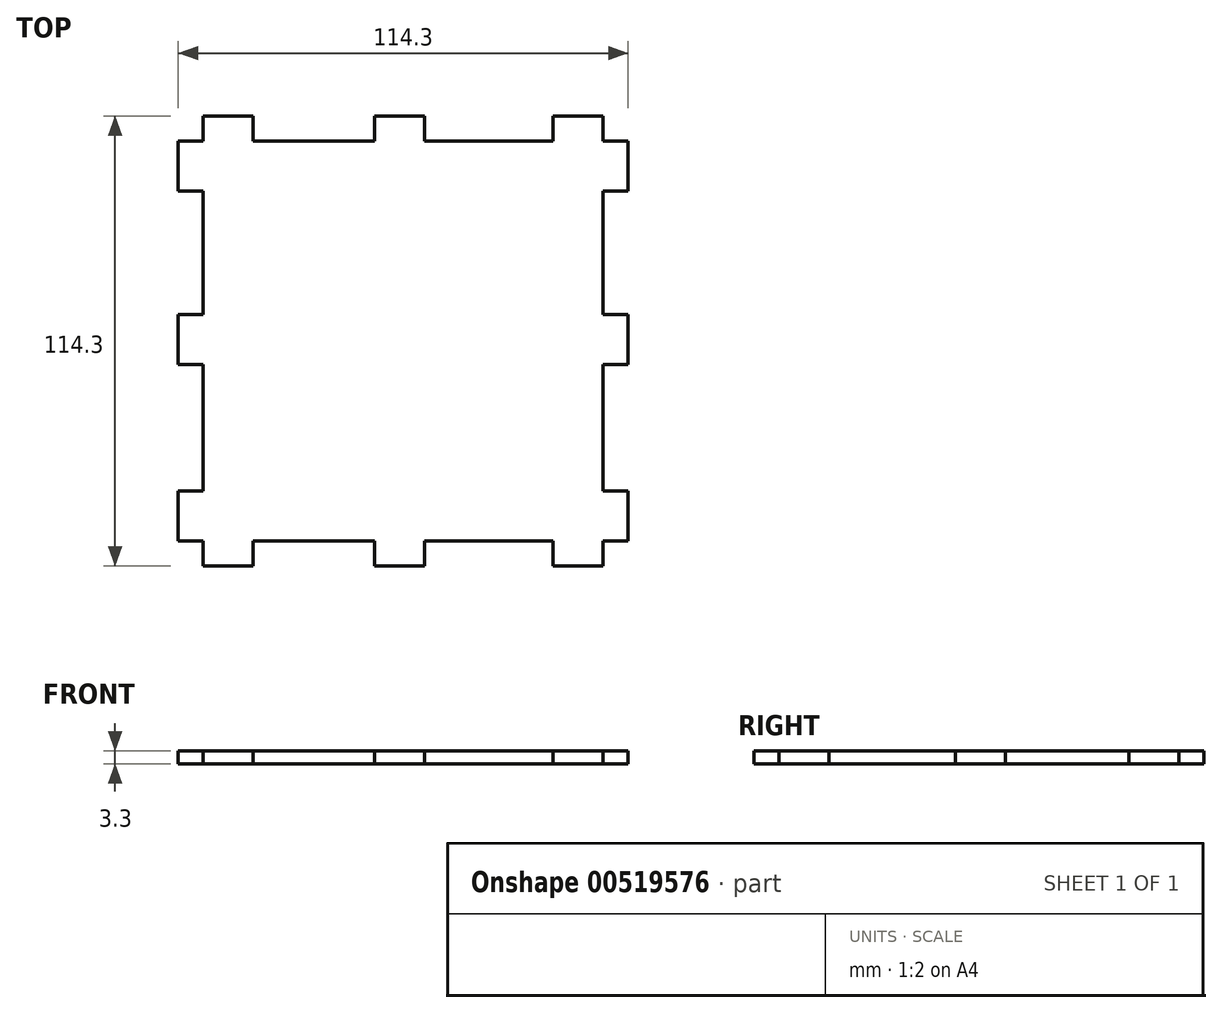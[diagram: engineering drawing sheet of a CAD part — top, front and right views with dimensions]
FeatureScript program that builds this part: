
annotation { "Feature Type Name" : "Feature", "Feature Type Description" : "" }
export const myFeature = defineFeature(function(context is Context, id is Id, definition is map)
    precondition{}
    {
        {
            var Q0;
            Q0=qCreatedBy(makeId("Top.planeOp"),FACE);
            var sketch = newSketch(context, id + "F0", { "sketchPlane" : qUnion([Q0])});
            skPoint(sketch, "E0.middle", {"position": v(0, 0) * mm});
            skPoint(sketch, "E0.top.end.orphan", {"position": v(-50.8, 50.8) * mm});
            skPoint(sketch, "E0.left.end.orphan", {"position": v(50.8, 50.8) * mm});
            skPoint(sketch, "E0.bottom.end.orphan", {"position": v(-50.8, -50.8) * mm});
            skPoint(sketch, "E0.bottom.start.orphan", {"position": v(50.8, -50.8) * mm});
            skLineSegment(sketch, "E1", {"start": v(-38.1, 50.8) * mm, "end": v(-7.3, 50.8) * mm});
            skLineSegment(sketch, "E2", {"start": v(50.8, 38.1) * mm, "end": v(50.8, 6.7) * mm});
            skLineSegment(sketch, "E3", {"start": v(38.1, -50.8) * mm, "end": v(5.4, -50.8) * mm});
            skLineSegment(sketch, "E4", {"start": v(-50.8, -38.1) * mm, "end": v(-50.8, -6) * mm});
            skLineSegment(sketch, "E5", {"start": v(-50.8, 50.8) * mm, "end": v(-50.8, 57.15) * mm});
            skLineSegment(sketch, "E6", {"start": v(-50.8, 57.15) * mm, "end": v(-38.1, 57.15) * mm});
            skLineSegment(sketch, "E7", {"start": v(-38.1, 57.15) * mm, "end": v(-38.1, 50.8) * mm});
            skPoint(sketch, "E8.start.orphan", {"position": v(0, 50.8) * mm});
            skLineSegment(sketch, "E9", {"start": v(-7.3, 57.15) * mm, "end": v(-7.3, 50.8) * mm});
            skPoint(sketch, "E10.end.orphan", {"position": v(5.4, 50.8) * mm});
            skPoint(sketch, "E11.start.orphan", {"position": v(5.4, 57.15) * mm});
            skLineSegment(sketch, "E12", {"start": v(-7.3, 57.15) * mm, "end": v(5.4, 57.15) * mm});
            skLineSegment(sketch, "E13", {"start": v(5.4, 57.15) * mm, "end": v(5.4, 50.8) * mm});
            skLineSegment(sketch, "E14.trimOffspring", {"start": v(5.4, 50.8) * mm, "end": v(38.1, 50.8) * mm});
            skLineSegment(sketch, "E15", {"start": v(50.8, 50.8) * mm, "end": v(50.8, 57.15) * mm});
            skLineSegment(sketch, "E16", {"start": v(50.8, 57.15) * mm, "end": v(38.1, 57.15) * mm});
            skLineSegment(sketch, "E17", {"start": v(38.1, 57.15) * mm, "end": v(38.1, 50.8) * mm});
            skLineSegment(sketch, "E18.MirrorCS", {"start": v(-50.8, -57.15) * mm, "end": v(-38.1, -57.15) * mm});
            skLineSegment(sketch, "E19.MirrorCS", {"start": v(-50.8, -50.8) * mm, "end": v(-50.8, -57.15) * mm});
            skLineSegment(sketch, "E20.MirrorCS", {"start": v(-38.1, -57.15) * mm, "end": v(-38.1, -50.8) * mm});
            skPoint(sketch, "E21.MirrorP", {"position": v(5.4, -50.8) * mm});
            skLineSegment(sketch, "E22.MirrorCS", {"start": v(50.8, -57.15) * mm, "end": v(38.1, -57.15) * mm});
            skLineSegment(sketch, "E23.MirrorCS", {"start": v(38.1, -57.15) * mm, "end": v(38.1, -50.8) * mm});
            skLineSegment(sketch, "E24.MirrorCS", {"start": v(50.8, -50.8) * mm, "end": v(50.8, -57.15) * mm});
            skLineSegment(sketch, "E25.trimOffspring", {"start": v(-7.3, -50.8) * mm, "end": v(-38.1, -50.8) * mm});
            skLineSegment(sketch, "E26", {"start": v(0, 0) * mm, "end": v(50.8, 0) * mm, "construction": true});
            skLineSegment(sketch, "E27", {"start": v(-50.8, 50.8) * mm, "end": v(-57.15, 50.8) * mm});
            skLineSegment(sketch, "E28", {"start": v(-57.15, 50.8) * mm, "end": v(-57.15, 38.1) * mm});
            skLineSegment(sketch, "E29", {"start": v(-57.15, 38.1) * mm, "end": v(-50.8, 38.1) * mm});
            skLineSegment(sketch, "E30", {"start": v(-57.15, 6.7) * mm, "end": v(-50.8, 6.7) * mm});
            skLineSegment(sketch, "E31", {"start": v(-57.15, -6) * mm, "end": v(-50.8, -6) * mm});
            skLineSegment(sketch, "E32", {"start": v(-50.8, -50.8) * mm, "end": v(-57.15, -50.8) * mm});
            skLineSegment(sketch, "E33", {"start": v(-57.15, -50.8) * mm, "end": v(-57.15, -38.1) * mm});
            skLineSegment(sketch, "E34", {"start": v(-57.15, -38.1) * mm, "end": v(-50.8, -38.1) * mm});
            skLineSegment(sketch, "E35.trimOffspring", {"start": v(-50.8, 6.7) * mm, "end": v(-50.8, 38.1) * mm});
            skPoint(sketch, "E36.orphan", {"position": v(-50.8, 0) * mm});
            skPoint(sketch, "E37.start.orphan", {"position": v(-57.15, 0) * mm});
            skLineSegment(sketch, "E38", {"start": v(-57.15, -6) * mm, "end": v(-57.15, 6.7) * mm});
            skLineSegment(sketch, "E39.MirrorCS", {"start": v(57.15, 50.8) * mm, "end": v(57.15, 38.1) * mm});
            skLineSegment(sketch, "E40.MirrorCS", {"start": v(50.8, 50.8) * mm, "end": v(57.15, 50.8) * mm});
            skLineSegment(sketch, "E41.MirrorCS", {"start": v(57.15, 38.1) * mm, "end": v(50.8, 38.1) * mm});
            skLineSegment(sketch, "E42.MirrorCS", {"start": v(57.15, 6.7) * mm, "end": v(50.8, 6.7) * mm});
            skLineSegment(sketch, "E43.MirrorCS", {"start": v(57.15, -6) * mm, "end": v(57.15, 6.7) * mm});
            skLineSegment(sketch, "E44.MirrorCS", {"start": v(57.15, -6) * mm, "end": v(50.8, -6) * mm});
            skLineSegment(sketch, "E45.MirrorCS", {"start": v(57.15, -38.1) * mm, "end": v(50.8, -38.1) * mm});
            skLineSegment(sketch, "E46.MirrorCS", {"start": v(57.15, -50.8) * mm, "end": v(57.15, -38.1) * mm});
            skLineSegment(sketch, "E47.MirrorCS", {"start": v(50.8, -50.8) * mm, "end": v(57.15, -50.8) * mm});
            skLineSegment(sketch, "E48.trimOffspring", {"start": v(50.8, -6) * mm, "end": v(50.8, -38.1) * mm});
            skPoint(sketch, "E49.MirrorCS.start.orphan", {"position": v(-7.3, -57.15) * mm});
            skPoint(sketch, "E50.MirrorCS.end.orphan", {"position": v(5.4, -57.15) * mm});
            skLineSegment(sketch, "E51", {"start": v(-7.3, -50.8) * mm, "end": v(-7.3, -57.15) * mm});
            skLineSegment(sketch, "E52", {"start": v(-7.3, -57.15) * mm, "end": v(5.4, -57.15) * mm});
            skLineSegment(sketch, "E53", {"start": v(5.4, -57.15) * mm, "end": v(5.4, -50.8) * mm});
            skSolve(sketch);
        }
        {
            var Q0;
            Q0 = qSketchRegion(id + "F0", true);
            extrude(context, id + "F1", {"entities" : qUnion([Q0]), "depth" : 3.3 * mm, "offsetDistance" : 25.4 * mm});
        }
    });
